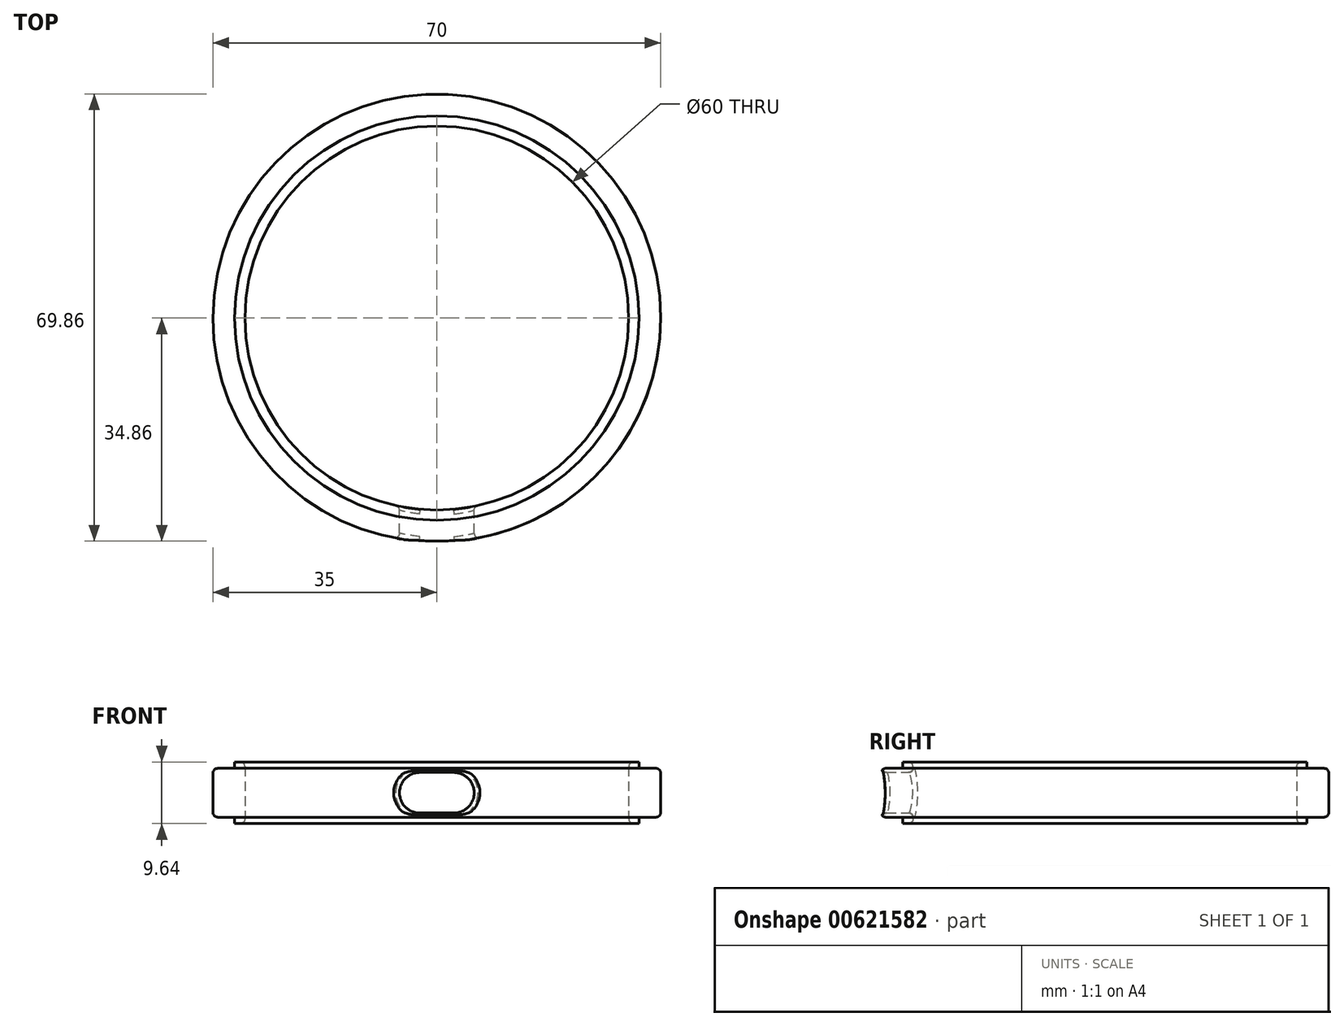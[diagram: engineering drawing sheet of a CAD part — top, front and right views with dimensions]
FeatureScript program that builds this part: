
annotation { "Feature Type Name" : "Feature", "Feature Type Description" : "" }
export const myFeature = defineFeature(function(context is Context, id is Id, definition is map)
    precondition{}
    {
        {
            var Q0;
            Q0=qCreatedBy(makeId("Top.planeOp"),FACE);
            var sketch = newSketch(context, id + "F0", { "sketchPlane" : qUnion([Q0])});
            skCircle(sketch, "E0", {"center": v(0, 0) * mm, "radius": 35 * mm});
            skCircle(sketch, "E1", {"center": v(0, 0) * mm, "radius": 30 * mm});
            skSolve(sketch);
        }
        {
            var Q0;
            Q0 = qSketchRegion(id + "F0", true);
            extrude(context, id + "F1", {"entities" : qUnion([Q0]), "endBound" : BoundingType.SYMMETRIC, "depth" : 7.63 * mm, "offsetDistance" : 25 * mm});
        }
        {
            var Q0;
            Q0=makeQuery(id+"F1.opExtrude","CAP_FACE",FACE,{"disambiguationData":[OSD([sQuery(id+"F0.wireOp",EDGE,"E0"),sQuery(id+"F0.wireOp",EDGE,"E1")])],"isStart":false});
            var sketch = newSketch(context, id + "F2", { "sketchPlane" : qUnion([Q0])});
            skCircle(sketch, "E2.0", {"center": v(0, 0) * mm, "radius": 30 * mm});
            skCircle(sketch, "E3", {"center": v(0, 0) * mm, "radius": 31.6 * mm});
            skSolve(sketch);
        }
        {
            var Q0;
            Q0 = qSketchRegion(id + "F2", true);
            extrude(context, id + "F3", {"entities" : qUnion([Q0]), "operationType" : NewBodyOperationType.ADD, "depth" : 1 * mm, "offsetDistance" : 25 * mm, "hasSecondDirection" : true, "secondDirectionOppositeDirection" : true, "secondDirectionDepth" : 8.63 * mm});
        }
        {
            var Q0;
            Q0=qCreatedBy(makeId("Front.planeOp"),FACE);
            var sketch = newSketch(context, id + "F4", { "sketchPlane" : qUnion([Q0])});
            skLineSegment(sketch, "E4", {"start": v(-2.67, 0) * mm, "end": v(2.67, 0) * mm});
            skArc(sketch, "E5.0.startCap", {"start": v(-2.67, -3.17) * mm, "mid": v(-5.84, 0) * mm, "end": v(-2.67, 3.17) * mm});
            skArc(sketch, "E5.0.endCap", {"start": v(2.66, 3.17) * mm, "mid": v(5.84, 0) * mm, "end": v(2.66, -3.17) * mm});
            skLineSegment(sketch, "E5.0.left", {"start": v(-2.66, 3.17) * mm, "end": v(2.66, 3.17) * mm});
            skLineSegment(sketch, "E5.0.right", {"start": v(-2.66, -3.17) * mm, "end": v(2.66, -3.17) * mm});
            skSolve(sketch);
        }
        {
            var Q0;
            Q0 = qSketchRegion(id + "F4", true);
            extrude(context, id + "F5", {"entities" : qUnion([Q0]), "operationType" : NewBodyOperationType.REMOVE, "endBound" : BoundingType.THROUGH_ALL, "depth" : 25 * mm, "offsetDistance" : 25 * mm});
        }
        {
            var Q0;
            Q0=makeQuery(id+"F3.boolean.opBoolean","MERGE",FACE,{"derivedFrom":[makeQuery(id+"F1.opExtrude","SWEPT_FACE",FACE,{"disambiguationData":[OSD([sQuery(id+"F0.wireOp",EDGE,"E1")])]}),makeQuery(id+"F3.opExtrude","SWEPT_FACE",FACE,{"disambiguationData":[OSD([sQuery(id+"F2.wireOp",EDGE,"E2.0")])]})]});
            var Q1;
            Q1=makeQuery(id+"F1.opExtrude","SWEPT_FACE",FACE,{"disambiguationData":[OSD([sQuery(id+"F0.wireOp",EDGE,"E0")])]});
            fillet(context, id + "F6", {"entities" : qUnion([Q0, Q1]), "radius" : .75 * mm, "tangentPropagation" : true, "allowEdgeOverflow" : false});
        }
    });
